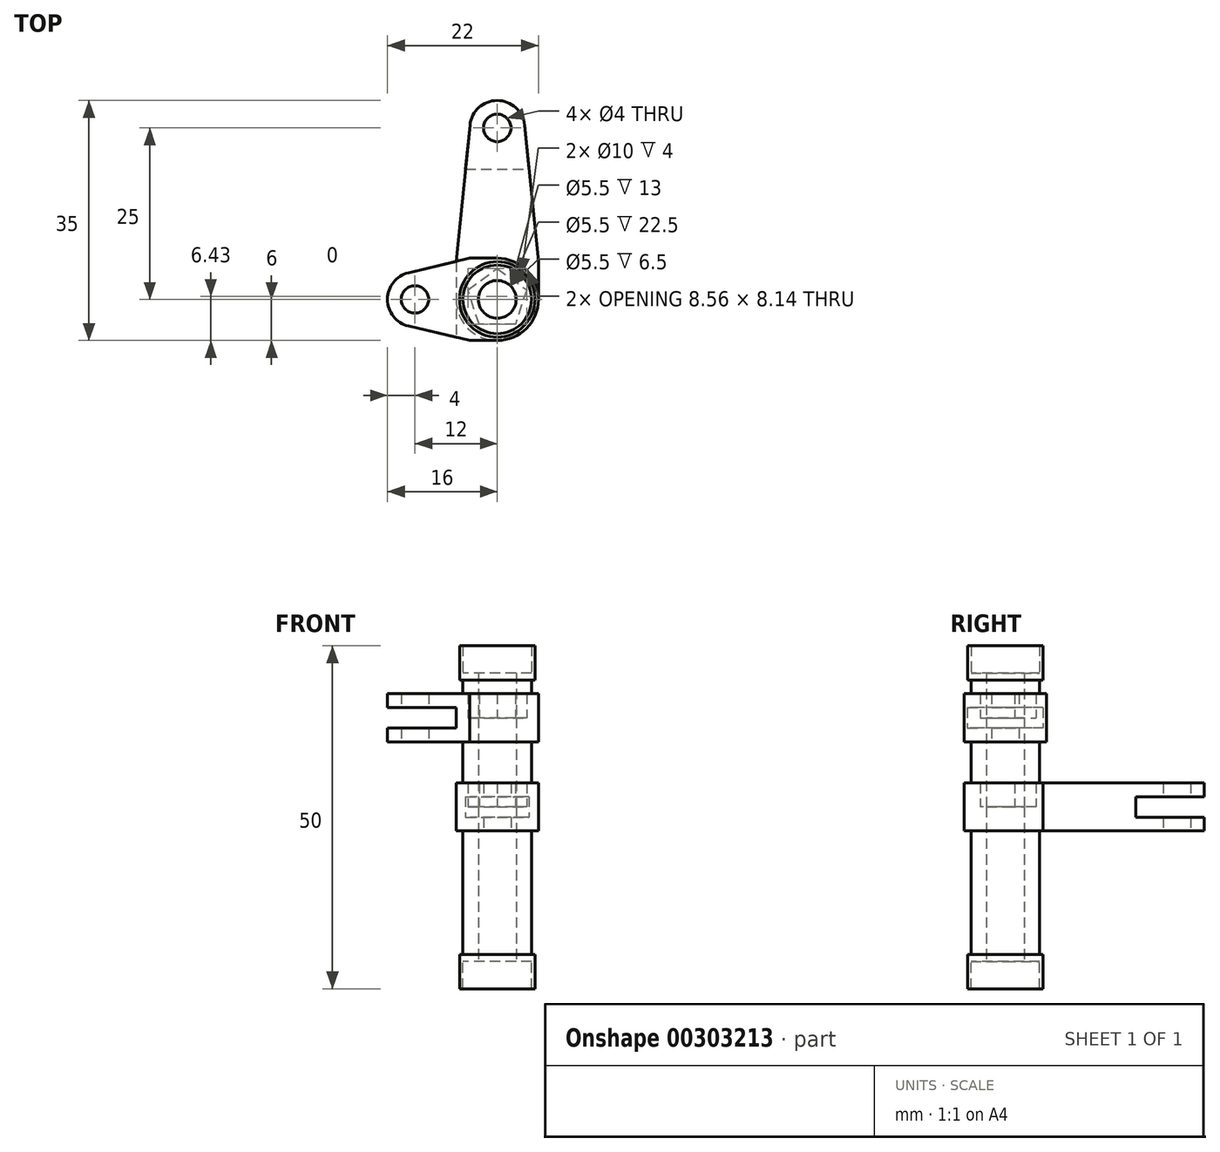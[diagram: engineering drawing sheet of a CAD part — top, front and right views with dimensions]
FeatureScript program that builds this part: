
annotation { "Feature Type Name" : "Feature", "Feature Type Description" : "" }
export const myFeature = defineFeature(function(context is Context, id is Id, definition is map)
    precondition{}
    {
        {
            var Q0;
            Q0=qCreatedBy(makeId("Top.planeOp"),FACE);
            var sketch = newSketch(context, id + "F0", { "sketchPlane" : qUnion([Q0])});
            skCircle(sketch, "E0", {"center": v(0, 0) * mm, "radius": 5.5 * mm});
            skCircle(sketch, "E1", {"center": v(0, 0) * mm, "radius": 5 * mm});
            skCircle(sketch, "E2", {"center": v(0, 0) * mm, "radius": 2.5 * mm});
            skCircle(sketch, "E3", {"center": v(0, 0) * mm, "radius": 4.5 * mm});
            skLineSegment(sketch, "E4", {"start": v(0, 6) * mm, "end": v(-4, 6) * mm});
            skLineSegment(sketch, "E5", {"start": v(0, -6) * mm, "end": v(-4, -6) * mm});
            skLineSegment(sketch, "E6", {"start": v(-4, 6) * mm, "end": v(-12.92, 3.9) * mm});
            skLineSegment(sketch, "E7", {"start": v(-4, -6) * mm, "end": v(-12.92, -3.9) * mm});
            skArc(sketch, "E8", {"start": v(-12.92, 3.9) * mm, "mid": v(-16, 0) * mm, "end": v(-12.92, -3.9) * mm});
            skCircle(sketch, "E9", {"center": v(-12, 0) * mm, "radius": 2 * mm});
            skCircle(sketch, "E10", {"center": v(0, 0) * mm, "radius": 2.75 * mm});
            skCircle(sketch, "E11", {"center": v(0, 0) * mm, "radius": 6 * mm});
            skCircle(sketch, "E12.cCircle", {"center": v(0, 0) * mm, "radius": 4.5 * mm, "construction": true});
            skLineSegment(sketch, "E12.0", {"start": v(0, 4.5) * mm, "end": v(4.28, 1.4) * mm});
            skLineSegment(sketch, "E12.1", {"start": v(4.28, 1.4) * mm, "end": v(2.65, -3.64) * mm});
            skLineSegment(sketch, "E12.2", {"start": v(2.65, -3.64) * mm, "end": v(-2.65, -3.64) * mm});
            skLineSegment(sketch, "E12.3", {"start": v(-2.65, -3.64) * mm, "end": v(-4.28, 1.4) * mm});
            skLineSegment(sketch, "E12.4", {"start": v(-4.28, 1.4) * mm, "end": v(0, 4.5) * mm});
            skLineSegment(sketch, "E13", {"start": v(-6, 5.53) * mm, "end": v(-6, -5.53) * mm});
            skLineSegment(sketch, "E14", {"start": v(6, 0) * mm, "end": v(6, -5.53) * mm});
            skLineSegment(sketch, "E15", {"start": v(-6, -5.53) * mm, "end": v(-3.98, -25.4) * mm, "construction": true});
            skLineSegment(sketch, "E16", {"start": v(6, -5.53) * mm, "end": v(3.98, -25.4) * mm, "construction": true});
            skArc(sketch, "E17", {"start": v(-3.98, -25.4) * mm, "mid": v(0, -29) * mm, "end": v(3.98, -25.4) * mm, "construction": true});
            skCircle(sketch, "E18", {"center": v(0, -25) * mm, "radius": 2 * mm, "construction": true});
            skLineSegment(sketch, "E19", {"start": v(-4.63, -19) * mm, "end": v(4.63, -19) * mm, "construction": true});
            skLineSegment(sketch, "E20.MirrorCS", {"start": v(-6, 5.53) * mm, "end": v(-3.98, 25.4) * mm});
            skLineSegment(sketch, "E21.MirrorCS", {"start": v(-4.63, 19) * mm, "end": v(4.63, 19) * mm});
            skArc(sketch, "E22.MirrorCS", {"start": v(-3.98, 25.4) * mm, "mid": v(0, 29) * mm, "end": v(3.98, 25.4) * mm});
            skLineSegment(sketch, "E23.MirrorCS", {"start": v(6, 0) * mm, "end": v(6, 5.53) * mm});
            skLineSegment(sketch, "E24.MirrorCS", {"start": v(6, 5.53) * mm, "end": v(3.98, 25.4) * mm});
            skCircle(sketch, "E25.MirrorC", {"center": v(0, 25) * mm, "radius": 2 * mm});
            skSolve(sketch);
        }
        {
            var Q0;
            Q0=makeQuery(id+"F0.imprint","IMPRINT",FACE,{"disambiguationData":[TD([[makeQuery(id+"F0.imprint","IMPRINT",EDGE,{"derivedFrom":sQuery(id+"F0.wireOp",EDGE,"E1")}),-1.0]])]});
            extrude(context, id + "F1", {"entities" : qUnion([Q0]), "depth" : 25 * mm, "hasSecondDirection" : true, "secondDirectionOppositeDirection" : false, "secondDirectionDepth" : 20 * mm});
        }
        {
            var Q0;
            {var subQ0=sQuery(id+"F0.wireOp",EDGE,"E12.4");Q0=makeQuery(id+"F0.imprint","IMPRINT",FACE,{"disambiguationData":[TD([[makeQuery(id+"F0.imprint","IMPRINT",EDGE,{"derivedFrom":subQ0}),1.0]])]});}
            var Q1;
            {var subQ0=sQuery(id+"F0.wireOp",EDGE,"E12.0");Q1=makeQuery(id+"F0.imprint","IMPRINT",FACE,{"disambiguationData":[TD([[makeQuery(id+"F0.imprint","IMPRINT",EDGE,{"derivedFrom":subQ0}),1.0]])]});}
            var Q2;
            {var subQ0=sQuery(id+"F0.wireOp",EDGE,"E12.1");Q2=makeQuery(id+"F0.imprint","IMPRINT",FACE,{"disambiguationData":[TD([[makeQuery(id+"F0.imprint","IMPRINT",EDGE,{"derivedFrom":subQ0}),1.0]])]});}
            var Q3;
            {var subQ0=sQuery(id+"F0.wireOp",EDGE,"E12.3");Q3=makeQuery(id+"F0.imprint","IMPRINT",FACE,{"disambiguationData":[TD([[makeQuery(id+"F0.imprint","IMPRINT",EDGE,{"derivedFrom":subQ0}),1.0]])]});}
            var Q4;
            {var subQ0=sQuery(id+"F0.wireOp",EDGE,"E12.2");Q4=makeQuery(id+"F0.imprint","IMPRINT",FACE,{"disambiguationData":[TD([[makeQuery(id+"F0.imprint","IMPRINT",EDGE,{"derivedFrom":subQ0}),1.0]])]});}
            var Q5;
            Q5=makeQuery(id+"F0.imprint","IMPRINT",FACE,{"disambiguationData":[TD([[makeQuery(id+"F0.imprint","IMPRINT",EDGE,{"derivedFrom":sQuery(id+"F0.wireOp",EDGE,"E10")}),-1.0]])]});
            var Q6;
            Q6=makeQuery(id+"F0.imprint","IMPRINT",FACE,{"disambiguationData":[TD([[makeQuery(id+"F0.imprint","IMPRINT",EDGE,{"derivedFrom":sQuery(id+"F0.wireOp",EDGE,"E1")}),1.0]])]});
            extrude(context, id + "F2", {"entities" : qUnion([Q0, Q1, Q2, Q3, Q4, Q5, Q6]), "operationType" : NewBodyOperationType.ADD, "depth" : 21 * mm, "hasSecondDirection" : true, "secondDirectionOppositeDirection" : false, "secondDirectionDepth" : 18 * mm});
        }
        {
            var Q0;
            Q0=makeQuery(id+"F0.imprint","IMPRINT",FACE,{"disambiguationData":[TD([[makeQuery(id+"F0.imprint","IMPRINT",EDGE,{"derivedFrom":sQuery(id+"F0.wireOp",EDGE,"E10")}),-1.0]])]});
            extrude(context, id + "F3", {"entities" : qUnion([Q0]), "operationType" : NewBodyOperationType.ADD, "depth" : 18 * mm, "hasSecondDirection" : true, "secondDirectionOppositeDirection" : false, "secondDirectionDepth" : 14.5 * mm});
        }
        {
            var Q0;
            {var subQ0=sQuery(id+"F0.wireOp",EDGE,"E12.3");Q0=makeQuery(id+"F0.imprint","IMPRINT",FACE,{"disambiguationData":[TD([[makeQuery(id+"F0.imprint","IMPRINT",EDGE,{"derivedFrom":subQ0}),1.0]])]});}
            var Q1;
            {var subQ0=sQuery(id+"F0.wireOp",EDGE,"E12.1");Q1=makeQuery(id+"F0.imprint","IMPRINT",FACE,{"disambiguationData":[TD([[makeQuery(id+"F0.imprint","IMPRINT",EDGE,{"derivedFrom":subQ0}),1.0]])]});}
            var Q2;
            {var subQ0=sQuery(id+"F0.wireOp",EDGE,"E8");Q2=makeQuery(id+"F0.imprint","IMPRINT",FACE,{"disambiguationData":[TD([[makeQuery(id+"F0.imprint","IMPRINT",EDGE,{"derivedFrom":subQ0}),1.0]])]});}
            var Q3;
            {var subQ0=sQuery(id+"F0.wireOp",EDGE,"E4");var subQ5=sQuery(id+"F0.wireOp",EDGE,"E11");var subQ6=makeQuery(id+"F0.imprint","INTERSECT",VERTEX,{"derivedFrom":[subQ0,subQ5]});Q3=makeQuery(id+"F0.imprint","IMPRINT",FACE,{"disambiguationData":[TD([[makeQuery(id+"F0.imprint","IMPRINT",EDGE,{"disambiguationData":[TD([[subQ6,-1.0]])],"derivedFrom":subQ5}),1.0]])]});}
            var Q4;
            {var subQ0=sQuery(id+"F0.wireOp",EDGE,"E4");var subQ5=sQuery(id+"F0.wireOp",EDGE,"E11");var subQ6=makeQuery(id+"F0.imprint","INTERSECT",VERTEX,{"derivedFrom":[subQ0,subQ5]});Q4=makeQuery(id+"F0.imprint","IMPRINT",FACE,{"disambiguationData":[TD([[makeQuery(id+"F0.imprint","IMPRINT",EDGE,{"disambiguationData":[TD([[subQ6,1.0]])],"derivedFrom":subQ5}),1.0]])]});}
            var Q5;
            {var subQ3=sQuery(id+"F0.wireOp",EDGE,"E13");Q5=makeQuery(id+"F0.imprint","IMPRINT",FACE,{"disambiguationData":[TD([[makeQuery(id+"F0.imprint","IMPRINT",EDGE,{"derivedFrom":subQ3}),1.0]])]});}
            var Q6;
            {var subQ0=sQuery(id+"F0.wireOp",EDGE,"E12.2");Q6=makeQuery(id+"F0.imprint","IMPRINT",FACE,{"disambiguationData":[TD([[makeQuery(id+"F0.imprint","IMPRINT",EDGE,{"derivedFrom":subQ0}),1.0]])]});}
            var Q7;
            {var subQ0=sQuery(id+"F0.wireOp",EDGE,"E12.0");Q7=makeQuery(id+"F0.imprint","IMPRINT",FACE,{"disambiguationData":[TD([[makeQuery(id+"F0.imprint","IMPRINT",EDGE,{"derivedFrom":subQ0}),1.0]])]});}
            var Q8;
            {var subQ0=sQuery(id+"F0.wireOp",EDGE,"E12.4");Q8=makeQuery(id+"F0.imprint","IMPRINT",FACE,{"disambiguationData":[TD([[makeQuery(id+"F0.imprint","IMPRINT",EDGE,{"derivedFrom":subQ0}),1.0]])]});}
            var Q9;
            Q9=makeQuery(id+"F0.imprint","IMPRINT",FACE,{"disambiguationData":[TD([[makeQuery(id+"F0.imprint","IMPRINT",EDGE,{"derivedFrom":sQuery(id+"F0.wireOp",EDGE,"E1")}),1.0]])]});
            var Q10;
            Q10=makeQuery(id+"F0.imprint","IMPRINT",FACE,{"disambiguationData":[TD([[makeQuery(id+"F0.imprint","IMPRINT",EDGE,{"derivedFrom":sQuery(id+"F0.wireOp",EDGE,"E1")}),-1.0]])]});
            extrude(context, id + "F4", {"entities" : qUnion([Q0, Q1, Q2, Q3, Q4, Q5, Q6, Q7, Q8, Q9, Q10]), "depth" : 18 * mm, "hasSecondDirection" : true, "secondDirectionOppositeDirection" : false, "secondDirectionDepth" : 11 * mm});
        }
        {
            var Q0;
            {var subQ4=sQuery(id+"F0.wireOp",EDGE,"E8");Q0=makeQuery(id+"F0.imprint","IMPRINT",FACE,{"disambiguationData":[TD([[makeQuery(id+"F0.imprint","IMPRINT",EDGE,{"derivedFrom":subQ4}),1.0]])]});}
            extrude(context, id + "F5", {"entities" : qUnion([Q0]), "operationType" : NewBodyOperationType.REMOVE, "depth" : 16 * mm, "hasSecondDirection" : true, "secondDirectionOppositeDirection" : false, "secondDirectionDepth" : 13 * mm});
        }
        {
            var Q0;
            Q0=makeQuery(id+"F0.imprint","IMPRINT",FACE,{"disambiguationData":[TD([[makeQuery(id+"F0.imprint","IMPRINT",EDGE,{"derivedFrom":sQuery(id+"F0.wireOp",EDGE,"E10")}),-1.0]])]});
            extrude(context, id + "F6", {"entities" : qUnion([Q0]), "depth" : 14.5 * mm, "hasSecondDirection" : true, "secondDirectionOppositeDirection" : false, "secondDirectionDepth" : 11 * mm});
        }
        {
            var Q0;
            {var subQ8=sQuery(id+"F0.wireOp",EDGE,"E1");var subQ9=makeQuery(id+"F0.imprint","INTERSECT",VERTEX,{"derivedFrom":[subQ8,sQuery(id+"F0.wireOp",EDGE,"aCzHrq4B-m7fe-IkVn-fX3y-AQXxxRyI4eLV")]});Q0=makeQuery(id+"F0.imprint","IMPRINT",FACE,{"disambiguationData":[TD([[makeQuery(id+"F0.imprint","IMPRINT",EDGE,{"disambiguationData":[TD([[subQ9,1.0]])],"derivedFrom":subQ8}),1.0]])]});}
            var Q1;
            {var subQ0=sQuery(id+"F0.wireOp",EDGE,"E12.0");Q1=makeQuery(id+"F0.imprint","IMPRINT",FACE,{"disambiguationData":[TD([[makeQuery(id+"F0.imprint","IMPRINT",EDGE,{"derivedFrom":subQ0}),1.0]])]});}
            var Q2;
            Q2=makeQuery(id+"F0.imprint","IMPRINT",FACE,{"disambiguationData":[TD([[makeQuery(id+"F0.imprint","IMPRINT",EDGE,{"derivedFrom":sQuery(id+"F0.wireOp",EDGE,"E10")}),-1.0]])]});
            var Q3;
            {var subQ0=sQuery(id+"F0.wireOp",EDGE,"E12.1");Q3=makeQuery(id+"F0.imprint","IMPRINT",FACE,{"disambiguationData":[TD([[makeQuery(id+"F0.imprint","IMPRINT",EDGE,{"derivedFrom":subQ0}),1.0]])]});}
            var Q4;
            {var subQ0=sQuery(id+"F0.wireOp",EDGE,"E12.4");Q4=makeQuery(id+"F0.imprint","IMPRINT",FACE,{"disambiguationData":[TD([[makeQuery(id+"F0.imprint","IMPRINT",EDGE,{"derivedFrom":subQ0}),1.0]])]});}
            var Q5;
            {var subQ0=sQuery(id+"F0.wireOp",EDGE,"E12.2");Q5=makeQuery(id+"F0.imprint","IMPRINT",FACE,{"disambiguationData":[TD([[makeQuery(id+"F0.imprint","IMPRINT",EDGE,{"derivedFrom":subQ0}),1.0]])]});}
            var Q6;
            {var subQ0=sQuery(id+"F0.wireOp",EDGE,"E12.3");Q6=makeQuery(id+"F0.imprint","IMPRINT",FACE,{"disambiguationData":[TD([[makeQuery(id+"F0.imprint","IMPRINT",EDGE,{"derivedFrom":subQ0}),1.0]])]});}
            extrude(context, id + "F7", {"entities" : qUnion([Q0, Q1, Q2, Q3, Q4, Q5, Q6]), "operationType" : NewBodyOperationType.ADD, "depth" : 11 * mm, "hasSecondDirection" : true, "secondDirectionOppositeDirection" : false, "secondDirectionDepth" : 5 * mm});
        }
        {
            var Q0;
            Q0=makeQuery(id+"F0.imprint","IMPRINT",FACE,{"disambiguationData":[TD([[makeQuery(id+"F0.imprint","IMPRINT",EDGE,{"derivedFrom":sQuery(id+"F0.wireOp",EDGE,"E10")}),-1.0]])]});
            extrude(context, id + "F8", {"entities" : qUnion([Q0]), "operationType" : NewBodyOperationType.ADD, "depth" : 5 * mm, "hasSecondDirection" : true, "secondDirectionOppositeDirection" : false, "secondDirectionDepth" : 1.5 * mm});
        }
        {
            var Q0;
            {var subQ0=sQuery(id+"F0.wireOp",EDGE,"E12.1");Q0=makeQuery(id+"F0.imprint","IMPRINT",FACE,{"disambiguationData":[TD([[makeQuery(id+"F0.imprint","IMPRINT",EDGE,{"derivedFrom":subQ0}),1.0]])]});}
            var Q1;
            Q1=makeQuery(id+"F0.imprint","IMPRINT",FACE,{"disambiguationData":[TD([[makeQuery(id+"F0.imprint","IMPRINT",EDGE,{"derivedFrom":sQuery(id+"F0.wireOp",EDGE,"E1")}),1.0]])]});
            var Q2;
            {var subQ0=sQuery(id+"F0.wireOp",EDGE,"E12.3");Q2=makeQuery(id+"F0.imprint","IMPRINT",FACE,{"disambiguationData":[TD([[makeQuery(id+"F0.imprint","IMPRINT",EDGE,{"derivedFrom":subQ0}),1.0]])]});}
            var Q3;
            {var subQ0=sQuery(id+"F0.wireOp",EDGE,"E12.4");Q3=makeQuery(id+"F0.imprint","IMPRINT",FACE,{"disambiguationData":[TD([[makeQuery(id+"F0.imprint","IMPRINT",EDGE,{"derivedFrom":subQ0}),1.0]])]});}
            var Q4;
            {var subQ0=sQuery(id+"F0.wireOp",EDGE,"E12.2");Q4=makeQuery(id+"F0.imprint","IMPRINT",FACE,{"disambiguationData":[TD([[makeQuery(id+"F0.imprint","IMPRINT",EDGE,{"derivedFrom":subQ0}),1.0]])]});}
            var Q5;
            Q5=makeQuery(id+"F0.imprint","IMPRINT",FACE,{"disambiguationData":[TD([[makeQuery(id+"F0.imprint","IMPRINT",EDGE,{"derivedFrom":sQuery(id+"F0.wireOp",EDGE,"E1")}),-1.0]])]});
            var Q6;
            {var subQ0=sQuery(id+"F0.wireOp",EDGE,"E12.0");Q6=makeQuery(id+"F0.imprint","IMPRINT",FACE,{"disambiguationData":[TD([[makeQuery(id+"F0.imprint","IMPRINT",EDGE,{"derivedFrom":subQ0}),1.0]])]});}
            var Q7;
            Q7=makeQuery(id+"F0.imprint","IMPRINT",FACE,{"disambiguationData":[TD([[makeQuery(id+"F0.imprint","IMPRINT",EDGE,{"derivedFrom":sQuery(id+"F0.wireOp",EDGE,"E0")}),-1.0]])]});
            var Q8;
            {var subQ0=sQuery(id+"F0.wireOp",EDGE,"E4");Q8=makeQuery(id+"F0.imprint","IMPRINT",FACE,{"disambiguationData":[TD([[makeQuery(id+"F0.imprint","IMPRINT",EDGE,{"derivedFrom":subQ0}),1.0]])]});}
            var Q9;
            {var subQ5=sQuery(id+"F0.wireOp",EDGE,"E4");Q9=makeQuery(id+"F0.imprint","IMPRINT",FACE,{"disambiguationData":[TD([[makeQuery(id+"F0.imprint","IMPRINT",EDGE,{"derivedFrom":subQ5}),-1.0]])]});}
            var Q10;
            {var subQ1=sQuery(id+"F0.wireOp",EDGE,"E21.MirrorCS");Q10=makeQuery(id+"F0.imprint","IMPRINT",FACE,{"disambiguationData":[TD([[makeQuery(id+"F0.imprint","IMPRINT",EDGE,{"derivedFrom":subQ1}),1.0]])]});}
            extrude(context, id + "F9", {"entities" : qUnion([Q0, Q1, Q2, Q3, Q4, Q5, Q6, Q7, Q8, Q9, Q10]), "depth" : 5 * mm, "hasSecondDirection" : true, "secondDirectionOppositeDirection" : true, "secondDirectionDepth" : 2 * mm});
        }
        {
            var Q0;
            {var subQ1=sQuery(id+"F0.wireOp",EDGE,"E21.MirrorCS");Q0=makeQuery(id+"F0.imprint","IMPRINT",FACE,{"disambiguationData":[TD([[makeQuery(id+"F0.imprint","IMPRINT",EDGE,{"derivedFrom":subQ1}),1.0]])]});}
            extrude(context, id + "F10", {"entities" : qUnion([Q0]), "operationType" : NewBodyOperationType.REMOVE, "depth" : 3 * mm});
        }
        {
            var Q0;
            Q0=makeQuery(id+"F0.imprint","IMPRINT",FACE,{"disambiguationData":[TD([[makeQuery(id+"F0.imprint","IMPRINT",EDGE,{"derivedFrom":sQuery(id+"F0.wireOp",EDGE,"E10")}),-1.0]])]});
            extrude(context, id + "F11", {"entities" : qUnion([Q0]), "depth" : 1.5 * mm, "hasSecondDirection" : true, "secondDirectionOppositeDirection" : true, "secondDirectionDepth" : 2 * mm});
        }
        {
            var Q0;
            {var subQ0=sQuery(id+"F0.wireOp",EDGE,"E12.2");Q0=makeQuery(id+"F0.imprint","IMPRINT",FACE,{"disambiguationData":[TD([[makeQuery(id+"F0.imprint","IMPRINT",EDGE,{"derivedFrom":subQ0}),1.0]])]});}
            var Q1;
            {var subQ0=sQuery(id+"F0.wireOp",EDGE,"E12.4");Q1=makeQuery(id+"F0.imprint","IMPRINT",FACE,{"disambiguationData":[TD([[makeQuery(id+"F0.imprint","IMPRINT",EDGE,{"derivedFrom":subQ0}),1.0]])]});}
            var Q2;
            {var subQ0=sQuery(id+"F0.wireOp",EDGE,"E12.3");Q2=makeQuery(id+"F0.imprint","IMPRINT",FACE,{"disambiguationData":[TD([[makeQuery(id+"F0.imprint","IMPRINT",EDGE,{"derivedFrom":subQ0}),1.0]])]});}
            var Q3;
            Q3=makeQuery(id+"F0.imprint","IMPRINT",FACE,{"disambiguationData":[TD([[makeQuery(id+"F0.imprint","IMPRINT",EDGE,{"derivedFrom":sQuery(id+"F0.wireOp",EDGE,"E1")}),1.0]])]});
            var Q4;
            Q4=makeQuery(id+"F0.imprint","IMPRINT",FACE,{"disambiguationData":[TD([[makeQuery(id+"F0.imprint","IMPRINT",EDGE,{"derivedFrom":sQuery(id+"F0.wireOp",EDGE,"E10")}),-1.0]])]});
            var Q5;
            {var subQ0=sQuery(id+"F0.wireOp",EDGE,"E12.0");Q5=makeQuery(id+"F0.imprint","IMPRINT",FACE,{"disambiguationData":[TD([[makeQuery(id+"F0.imprint","IMPRINT",EDGE,{"derivedFrom":subQ0}),1.0]])]});}
            var Q6;
            {var subQ0=sQuery(id+"F0.wireOp",EDGE,"E12.1");Q6=makeQuery(id+"F0.imprint","IMPRINT",FACE,{"disambiguationData":[TD([[makeQuery(id+"F0.imprint","IMPRINT",EDGE,{"derivedFrom":subQ0}),1.0]])]});}
            extrude(context, id + "F12", {"entities" : qUnion([Q0, Q1, Q2, Q3, Q4, Q5, Q6]), "operationType" : NewBodyOperationType.ADD, "oppositeDirection" : true, "depth" : 21 * mm, "hasSecondDirection" : true, "secondDirectionOppositeDirection" : true, "secondDirectionDepth" : 2 * mm});
        }
        {
            var Q0;
            Q0=makeQuery(id+"F0.imprint","IMPRINT",FACE,{"disambiguationData":[TD([[makeQuery(id+"F0.imprint","IMPRINT",EDGE,{"derivedFrom":sQuery(id+"F0.wireOp",EDGE,"E1")}),-1.0]])]});
            extrude(context, id + "F13", {"entities" : qUnion([Q0]), "operationType" : NewBodyOperationType.ADD, "oppositeDirection" : true, "depth" : 25 * mm, "hasSecondDirection" : true, "secondDirectionOppositeDirection" : true, "secondDirectionDepth" : 20 * mm});
        }
    });
